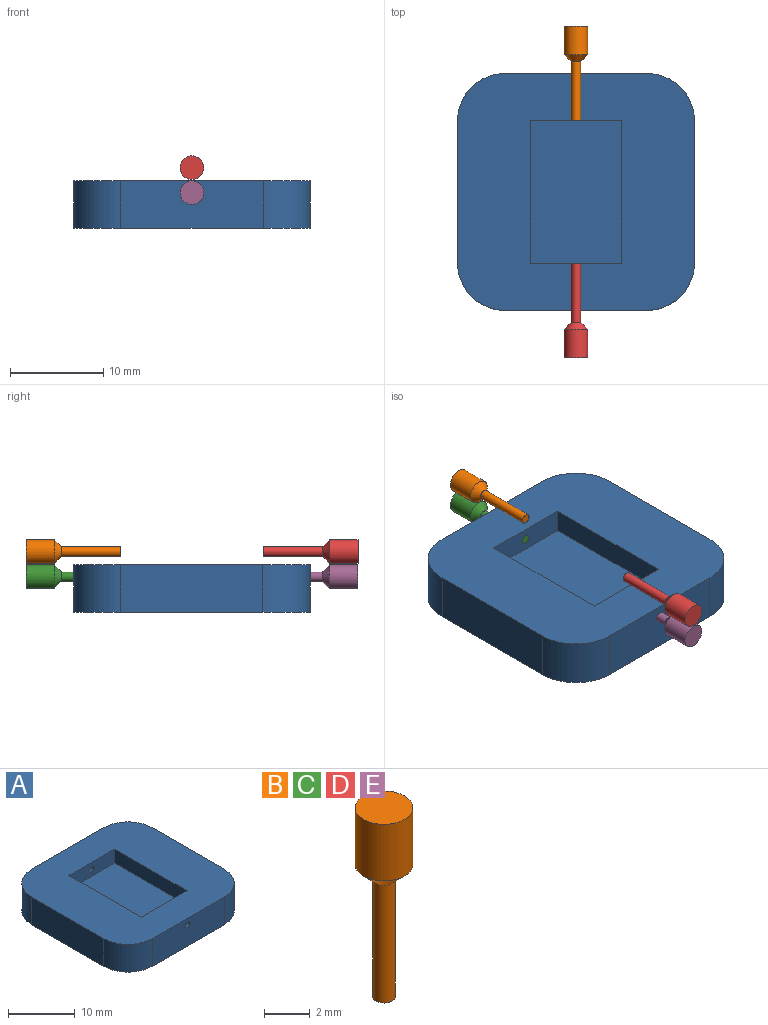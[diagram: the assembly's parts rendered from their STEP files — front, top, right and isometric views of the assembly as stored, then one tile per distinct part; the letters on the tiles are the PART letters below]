
ASSEMBLY  parts=5 mates=1
PART A: 17 faces, bbox 25.4x25.4x5.1 mm
  f0: plane 25.4x25.4mm, normal (0,0,1), area 475mm2, adj f1,f2,f3,f4,f6,f7,f8,f9
  f1: plane 15.24x5.08mm, normal (0,1,0), area 76.6mm2, adj f0,f5,f6,f9,f15
  f2: plane 15.24x5.08mm, normal (-1,0,0), area 77.4mm2, adj f0,f5,f6,f7
  f3: plane 15.24x5.08mm, normal (0,-1,0), area 76.6mm2, adj f0,f5,f7,f8,f16
  f4: plane 15.24x5.08mm, normal (1,0,0), area 77.4mm2, adj f0,f5,f8,f9
  f5: plane 25.4x25.4mm, normal (0,0,-1), area 623mm2, adj f1,f2,f3,f4,f6,f7,f8,f9
  f6: cylinder r=5.08mm len=5.08mm, axis (0,0,1), area 40.5mm2, adj f0,f1,f2,f5
  f7: cylinder r=5.08mm len=5.08mm, axis (0,0,-1), area 40.5mm2, adj f0,f2,f3,f5
  f8: cylinder r=5.08mm len=5.08mm, axis (0,0,1), area 40.5mm2, adj f0,f3,f4,f5
  f9: cylinder r=5.08mm len=5.08mm, axis (0,0,-1), area 40.5mm2, adj f0,f1,f4,f5
  f10: plane 15.27x2.54mm, normal (-1,0,0), area 38.8mm2, adj f0,f11,f13,f14
  f11: plane 9.69x2.54mm, normal (0,-1,0), area 23.8mm2, adj f0,f10,f12,f14,f15
  f12: plane 15.27x2.54mm, normal (1,0,0), area 38.8mm2, adj f0,f11,f13,f14
  f13: plane 9.69x2.54mm, normal (0,1,0), area 23.8mm2, adj f0,f10,f12,f14,f16
  f14: plane 15.27x9.69mm, normal (0,0,1), area 148mm2, adj f10,f11,f12,f13
  f15: cylinder r=0.5mm len=5.06mm, axis (0,-1,0), area 15.9mm2, adj f1,f11
  f16: cylinder r=0.5mm len=5.06mm, axis (0,1,0), area 15.9mm2, adj f3,f13
PART B: 6 faces, bbox 2.5x2.5x10.2 mm
  f0: cylinder r=0.5mm len=6.35mm, axis (0,0,-1), area 20mm2, adj f1,f3
  f1: plane 1x1mm, normal (0,0,-1), area 0.8mm2, adj f0
  f2: cylinder r=1.27mm len=3.05mm, axis (0,0,1), area 24.3mm2, adj f4,f5
  f3: plane 1.02x1.02mm, normal (0,0,-1), area 0mm2, adj f0,f5
  f4: plane 2.54x2.54mm, normal (0,0,1), area 5.1mm2, adj f2
  f5: cone r=1.27mm half-angle=45deg, axis (0,0,1), area 6mm2, adj f2,f3
PART C: same geometry as B
PART D: same geometry as B
PART E: same geometry as B
PLACE A t=(-0.65,-2.7,-2.66)mm
PLACE B rot(axis=(-1,0,0),90deg) t=(-59.08,7.56,-0.01)mm
PLACE C rot(axis=(-1,0,0),90deg) t=(-59.07,7.58,-2.69)mm
PLACE D rot(axis=(1,0,0),90deg) t=(-59.08,-7.72,7.68)mm
PLACE E rot(axis=(1,0,0),90deg) t=(-59.07,-7.7,5)mm
MATE fastened E.f0 <-> A.f15  axis (0,1,0) through (0.03,-7.7,1.15)mm
